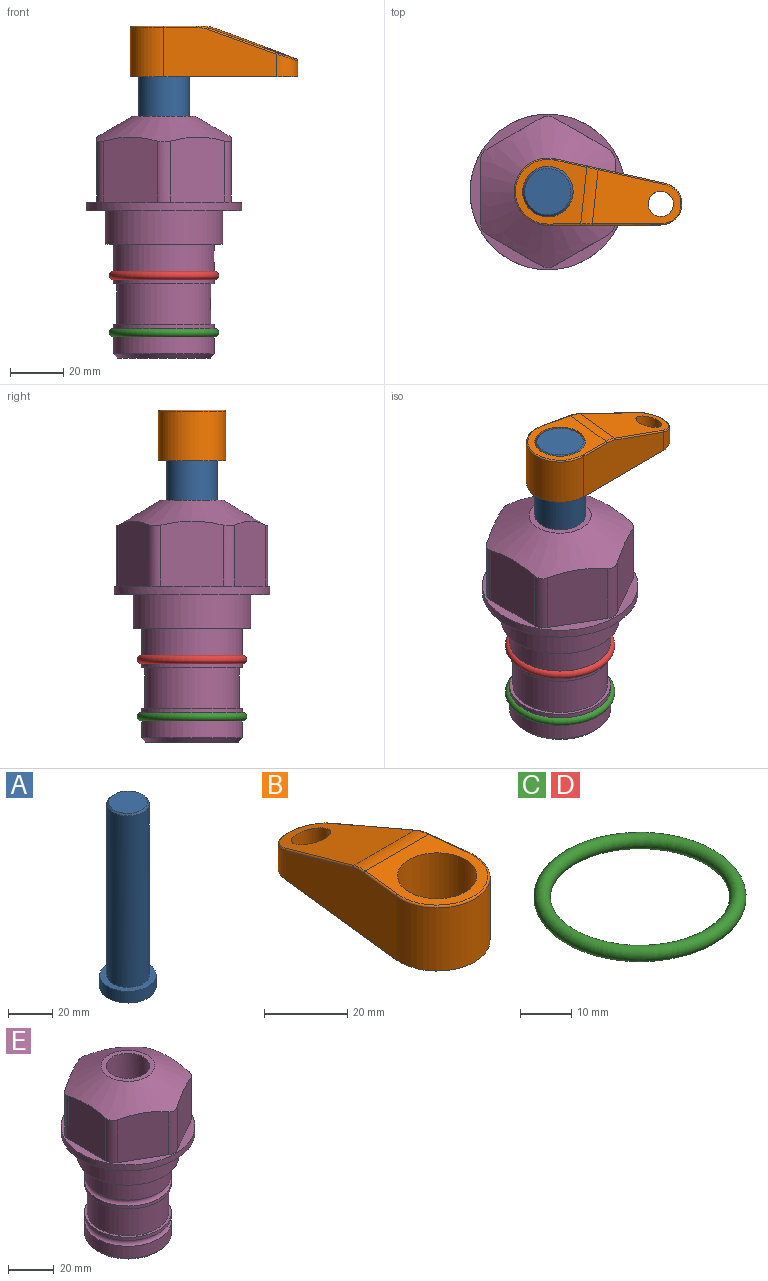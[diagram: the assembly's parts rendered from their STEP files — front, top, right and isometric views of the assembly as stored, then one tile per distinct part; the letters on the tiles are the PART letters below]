
ASSEMBLY  parts=5 mates=3
PART A: 6 faces, bbox 25.4x25.4x101.6 mm
  f0: plane 17.46x17.46mm, normal (0,0,1), area 239.5mm2, adj f5
  f1: plane 25.4x25.4mm, normal (0,0,-1), area 506.7mm2, adj f2
  f2: cylinder r=12.7mm len=25.4mm, axis (0,0,1), area 506.7mm2, adj f1,f3
  f3: plane 25.4x25.4mm, normal (0,0,1), area 221.7mm2, adj f2,f4
  f4: cylinder r=9.53mm len=94.46mm, axis (0,0,1), area 5653mm2, adj f3,f5
  f5: cone r=8.73mm half-angle=45deg, axis (0,0,-1), area 64.4mm2, adj f0,f4
PART B: 44 faces, bbox 27.5x64.5x19.1 mm
  f0: plane 2.3x0.95mm, normal (0,0,-1), area 1mm2, adj f25,f30,f34
  f1: plane 63.5x25.4mm, normal (0,0,-1), area 561.7mm2, adj f2,f3,f4,f5,f6,f7,f19,f20
  f2: cylinder r=12.7mm len=25.4mm, axis (0,0,-1), area 792.2mm2, adj f1,f3,f5,f13
  f3: plane 42.33x18.54mm, normal (0.99,0.11,0), area 647mm2, adj f1,f2,f4,f11,f12,f14
  f4: cylinder r=7.94mm len=15.78mm, axis (0,0,-1), area 158.6mm2, adj f1,f3,f5,f16
  f5: plane 42.33x18.54mm, normal (-0.99,0.11,0), area 647mm2, adj f1,f2,f4,f15,f17,f18
  f6: cylinder r=9.53mm len=19.05mm, axis (0,0,-1), area 1140.1mm2, adj f1,f8
  f7: cylinder r=4.76mm len=10.98mm, axis (0,0,-1), area 276.1mm2, adj f1,f9
  f8: plane 25.83x24.38mm, normal (0,0,1), area 262.2mm2, adj f6,f10,f11,f13,f15
  f9: plane 32.49x20.55mm, normal (0,0.34,0.94), area 489.9mm2, adj f7,f10,f14,f16,f18
  f10: cylinder r=12.7mm len=21.49mm, axis (-1,0,0), area 93.2mm2, adj f8,f9,f12,f17
  f11: cylinder r=0.51mm len=12.34mm, axis (0.11,-0.99,0), area 9.9mm2, adj f3,f8,f12,f13
  f12: bspline ~7.62x1.64mm, area 3.5mm2, adj f3,f10,f11,f14
  f13: torus R=12.19mm, axis (0,0,1), area 33.6mm2, adj f2,f8,f11,f15
  f14: cylinder r=0.51mm len=26.01mm, axis (0.1,-0.93,0.34), area 21.6mm2, adj f3,f9,f12,f16
  f15: cylinder r=0.51mm len=12.34mm, axis (0.11,0.99,0), area 9.9mm2, adj f5,f8,f13,f17
  f16: bspline ~15.78x7.05mm, area 15.7mm2, adj f4,f9,f14,f18
  f17: bspline ~7.62x1.64mm, area 3.5mm2, adj f5,f10,f15,f18
  f18: cylinder r=0.51mm len=26.01mm, axis (0.1,0.93,-0.34), area 21.6mm2, adj f5,f9,f16,f17
  f19: plane 21.6x14.29mm, normal (-0.99,-0.11,0), area 242.6mm2, adj f1,f26,f28,f34,f36,f38
  f20: plane 21.6x14.29mm, normal (0.99,-0.11,0), area 242.6mm2, adj f1,f27,f29,f37,f39,f41
  f21: cylinder r=12.7mm len=14.29mm, axis (0,0,-1), area 173.2mm2, adj f1,f26,f27,f30,f31,f33
  f22: cylinder r=7.94mm len=7.63mm, axis (0,0,-1), area 53.8mm2, adj f1,f28,f29,f42
  f23: plane 2.3x0.95mm, normal (0,0,-1), area 1mm2, adj f25,f33,f37
  f24: plane 17.94x12.32mm, normal (0,-0.34,-0.94), area 191.2mm2, adj f25,f38,f41,f42
  f25: cylinder r=9.53mm len=12.93mm, axis (-1,0,0), area 37.5mm2, adj f0,f23,f24,f31,f36,f39
  f26: cylinder r=1.59mm len=14.29mm, axis (0,0,-1), area 49mm2, adj f1,f19,f21,f32
  f27: cylinder r=1.59mm len=14.29mm, axis (0,0,-1), area 49mm2, adj f1,f20,f21,f35
  f28: cylinder r=1.59mm len=7.28mm, axis (0,0,-1), area 22.1mm2, adj f1,f19,f22,f40
  f29: cylinder r=1.59mm len=7.28mm, axis (0,0,-1), area 22.1mm2, adj f1,f20,f22,f43
  f30: torus R=14.29mm, axis (0,0,1), area 5.8mm2, adj f0,f21,f31,f32
  f31: bspline ~11.06x2.73mm, area 20.8mm2, adj f21,f25,f30,f33
  f32: sphere r=1.59mm, area 5.4mm2, adj f26,f30,f34
  f33: torus R=14.29mm, axis (0,0,1), area 5.8mm2, adj f21,f23,f31,f35
  f34: cylinder r=1.59mm len=1.68mm, axis (-0.11,0.99,0), area 2.4mm2, adj f0,f19,f32,f36
  f35: sphere r=1.59mm, area 5.4mm2, adj f27,f33,f37
  f36: bspline ~5.82x2.33mm, area 7.7mm2, adj f19,f25,f34,f38
  f37: cylinder r=1.59mm len=1.68mm, axis (0.11,0.99,0), area 2.4mm2, adj f20,f23,f35,f39
  f38: cylinder r=1.59mm len=18.33mm, axis (0.1,-0.93,0.34), area 46.7mm2, adj f19,f24,f36,f40
  f39: bspline ~5.82x2.33mm, area 7.7mm2, adj f20,f25,f37,f41
  f40: sphere r=1.59mm, area 3.6mm2, adj f28,f38,f42
  f41: cylinder r=1.59mm len=18.33mm, axis (0.1,0.93,-0.34), area 46.7mm2, adj f20,f24,f39,f43
  f42: bspline ~8.31x1.84mm, area 15.3mm2, adj f22,f24,f40,f43
  f43: sphere r=1.59mm, area 3.6mm2, adj f29,f41,f42
PART C: 1 faces, bbox 44.7x44.7x3.2 mm
  f0: torus R=19.05mm, axis (0,0,1), area 1193.9mm2
PART D: same geometry as C
PART E: 36 faces, bbox 58.7x58.7x91.2 mm
  f0: cylinder r=17.78mm len=35.56mm, axis (0,0,1), area 1670.8mm2, adj f23,f24,f31
  f1: cylinder r=19.05mm len=38.1mm, axis (0,0,1), area 1191.9mm2, adj f26,f27,f30
  f2: plane 58.66x58.66mm, normal (0,0,-1), area 1150.6mm2, adj f3,f28
  f3: cylinder r=29.33mm len=58.66mm, axis (0,0,-1), area 585.1mm2, adj f2,f4
  f4: plane 58.66x58.66mm, normal (0,0,1), area 475.9mm2, adj f3,f5,f6,f7,f8,f9,f10,f11
  f5: plane 24.5x20.32mm, normal (-0.5,0.87,0), area 562.8mm2, adj f4,f15,f16,f17
  f6: plane 24.5x20.32mm, normal (0.5,0.87,0), area 562.8mm2, adj f4,f14,f15,f17
  f7: plane 24.5x23.48mm, normal (1,0,0), area 562.8mm2, adj f4,f13,f14,f17
  f8: plane 24.5x20.32mm, normal (0.5,-0.87,0), area 562.8mm2, adj f4,f12,f13,f17
  f9: plane 24.5x20.32mm, normal (-0.5,-0.87,0), area 562.8mm2, adj f4,f11,f12,f17
  f10: plane 24.5x23.48mm, normal (-1,0,0), area 562.8mm2, adj f4,f11,f16,f17
  f11: cylinder r=5.08mm len=23.01mm, axis (0,0,-1), area 121.2mm2, adj f4,f9,f10,f17
  f12: cylinder r=5.08mm len=23.01mm, axis (0,0,-1), area 121.2mm2, adj f4,f8,f9,f17
  f13: cylinder r=5.08mm len=23.01mm, axis (0,0,-1), area 121.2mm2, adj f4,f7,f8,f17
  f14: cylinder r=5.08mm len=23.01mm, axis (0,0,-1), area 121.2mm2, adj f4,f6,f7,f17
  f15: cylinder r=5.08mm len=23.01mm, axis (0,0,-1), area 121.2mm2, adj f4,f5,f6,f17
  f16: cylinder r=5.08mm len=23.01mm, axis (0,0,-1), area 121.2mm2, adj f4,f5,f10,f17
  f17: cone r=11.73mm half-angle=60deg, axis (0,0,-1), area 2071.8mm2, adj f5,f6,f7,f8,f9,f10,f11,f12
  f18: plane 23.46x23.46mm, normal (0,0,1), area 147.4mm2, adj f17,f35
  f19: plane 34.93x34.93mm, normal (0,0,-1), area 958mm2, adj f29
  f20: cylinder r=19.05mm len=38.1mm, axis (0,0,1), area 760.1mm2, adj f21,f29
  f21: torus R=19.05mm, axis (0,0,1), area 565.3mm2, adj f20,f22
  f22: cylinder r=19.05mm len=38.1mm, axis (0,0,1), area 190mm2, adj f21,f23
  f23: plane 38.1x38.1mm, normal (0,0,1), area 146.9mm2, adj f0,f22
  f24: plane 38.1x38.1mm, normal (0,0,-1), area 146.9mm2, adj f0,f25
  f25: cylinder r=19.05mm len=38.1mm, axis (0,0,1), area 190mm2, adj f24,f26
  f26: torus R=19.05mm, axis (0,0,1), area 565.3mm2, adj f1,f25
  f27: plane 44.45x44.45mm, normal (0,0,-1), area 411.7mm2, adj f1,f28
  f28: cylinder r=22.23mm len=44.45mm, axis (0,0,1), area 1773.5mm2, adj f2,f27
  f29: cone r=19.05mm half-angle=45deg, axis (0,0,1), area 257.5mm2, adj f19,f20
  f30: cylinder r=3.17mm len=6.75mm, axis (-1,0,0), area 128mm2, adj f1,f33
  f31: cylinder r=3.17mm len=6.35mm, axis (-1,0,0), area 102.5mm2, adj f0,f33
  f32: plane 25.4x25.4mm, normal (0,0,1), area 506.7mm2, adj f33
  f33: cylinder r=12.7mm len=66.42mm, axis (0,0,-1), area 5236.2mm2, adj f30,f31,f32,f34
  f34: cone r=9.53mm half-angle=30deg, axis (0,0,-1), area 443.4mm2, adj f33,f35
  f35: cylinder r=9.53mm len=19.05mm, axis (0,0,-1), area 849mm2, adj f18,f34
PLACE A rot(axis=(0,0,-1),6.2deg) t=(0,0,-4.06)mm
PLACE B rot(axis=(0,0,-1),96.2deg) t=(0,0,50.55)mm
PLACE C t=(0,0,-21.59)mm
PLACE D at identity
PLACE E at identity fixed
MATE fastened C.f0 <-> E.f0  axis (0,0,1) through (0,0,-46.1)mm
MATE cylindrical A.f2 <-> E.f0  axis (0,0,1) through (0,0,21.58)mm
MATE fastened B.f2 <-> A.f2  axis (0,0,1) through (0,0,69.6)mm
